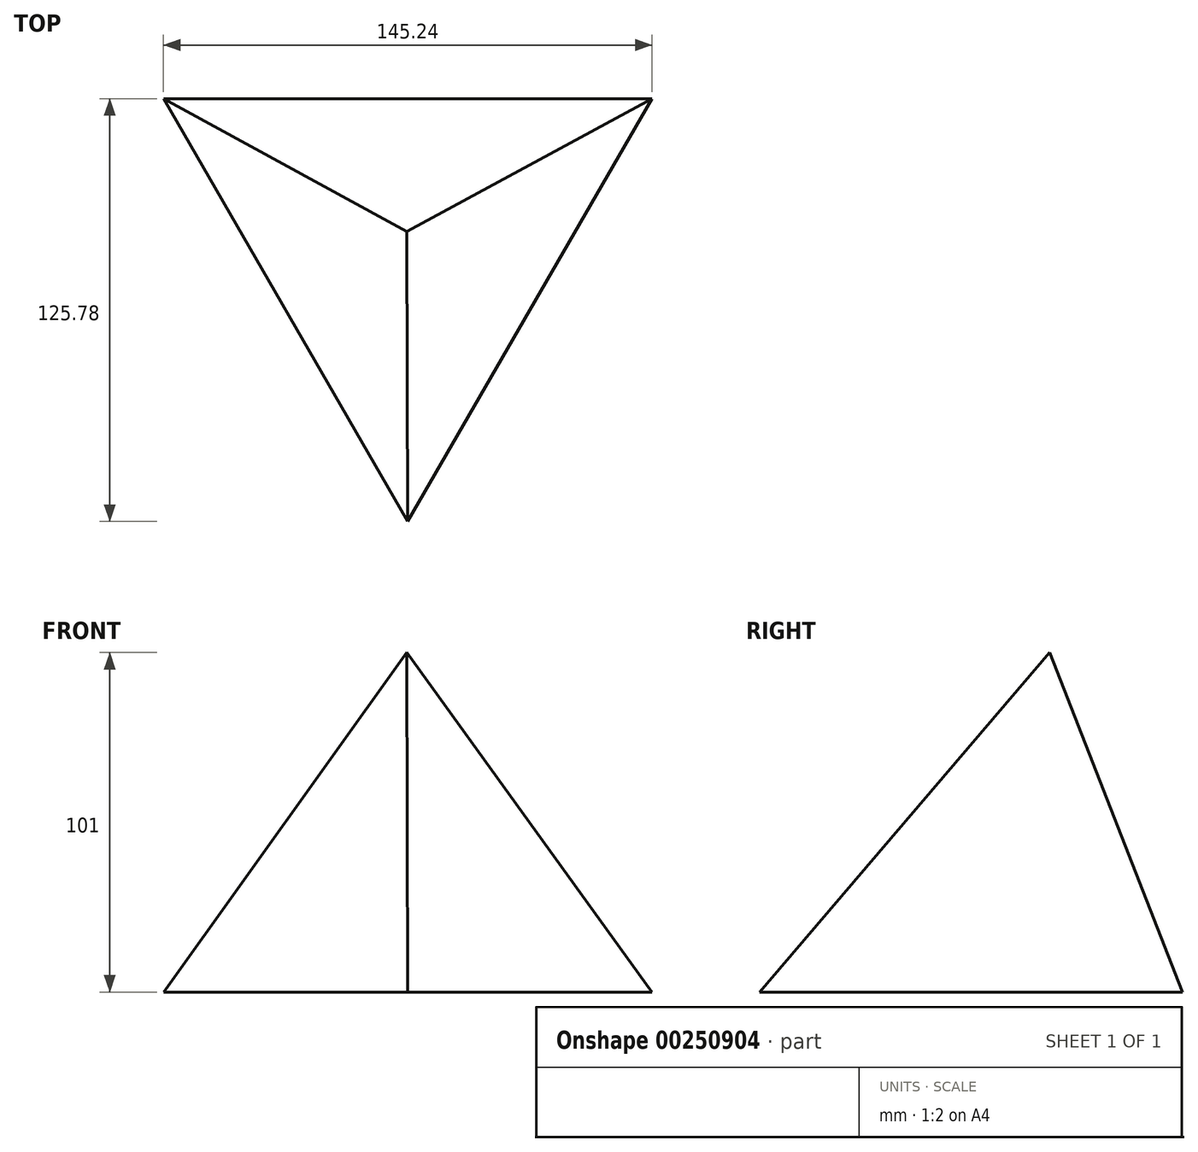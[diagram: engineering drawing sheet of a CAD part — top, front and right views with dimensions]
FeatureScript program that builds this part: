
annotation { "Feature Type Name" : "Feature", "Feature Type Description" : "" }
export const myFeature = defineFeature(function(context is Context, id is Id, definition is map)
    precondition{}
    {
        {
            var Q0;
            Q0=qCreatedBy(makeId("Top.planeOp"),FACE);
            var sketch = newSketch(context, id + "F0", { "sketchPlane" : qUnion([Q0])});
            skCircle(sketch, "E0.cCircle", {"center": v(0, 0) * mm, "radius": 83.85 * mm, "construction": true});
            skLineSegment(sketch, "E0.0", {"start": v(0, -83.85) * mm, "end": v(-72.62, 41.93) * mm});
            skLineSegment(sketch, "E0.1", {"start": v(-72.62, 41.93) * mm, "end": v(72.62, 41.93) * mm});
            skLineSegment(sketch, "E0.2", {"start": v(72.62, 41.93) * mm, "end": v(0, -83.85) * mm});
            skSolve(sketch);
        }
        {
            var Q0;
            Q0=qCreatedBy(makeId("Top.planeOp"),FACE);
            cPlane(context, id + "F1", {"entities" : qUnion([Q0]), "cplaneType" : CPlaneType.OFFSET, "offset" : 101 * mm, "width" : 150 * mm, "height" : 150 * mm});
        }
        {
            var Q0;
            Q0=qCreatedBy(id+"F1.planeOp",FACE);
            var sketch = newSketch(context, id + "F2", { "sketchPlane" : qUnion([Q0])});
            skPoint(sketch, "E1", {"position": v(-0.32, 2.4) * mm});
            skSolve(sketch);
        }
        {
            var Q0;
            Q0=sQuery(id+"F2.wireOp",VERTEX,"E1");
            var Q1;
            Q1=makeQuery(id+"F0.imprint","IMPRINT",FACE,{"disambiguationData":[TD([[makeQuery(id+"F0.imprint","IMPRINT",EDGE,{"derivedFrom":sQuery(id+"F0.wireOp",EDGE,"E0.0")}),-1.0]])]});
            loft(context, id + "F3", {"sheetProfilesArray" : [{ "sheetProfileEntities" : qUnion([Q0]) }, { "sheetProfileEntities" : qUnion([Q1]) }]});
        }
    });
